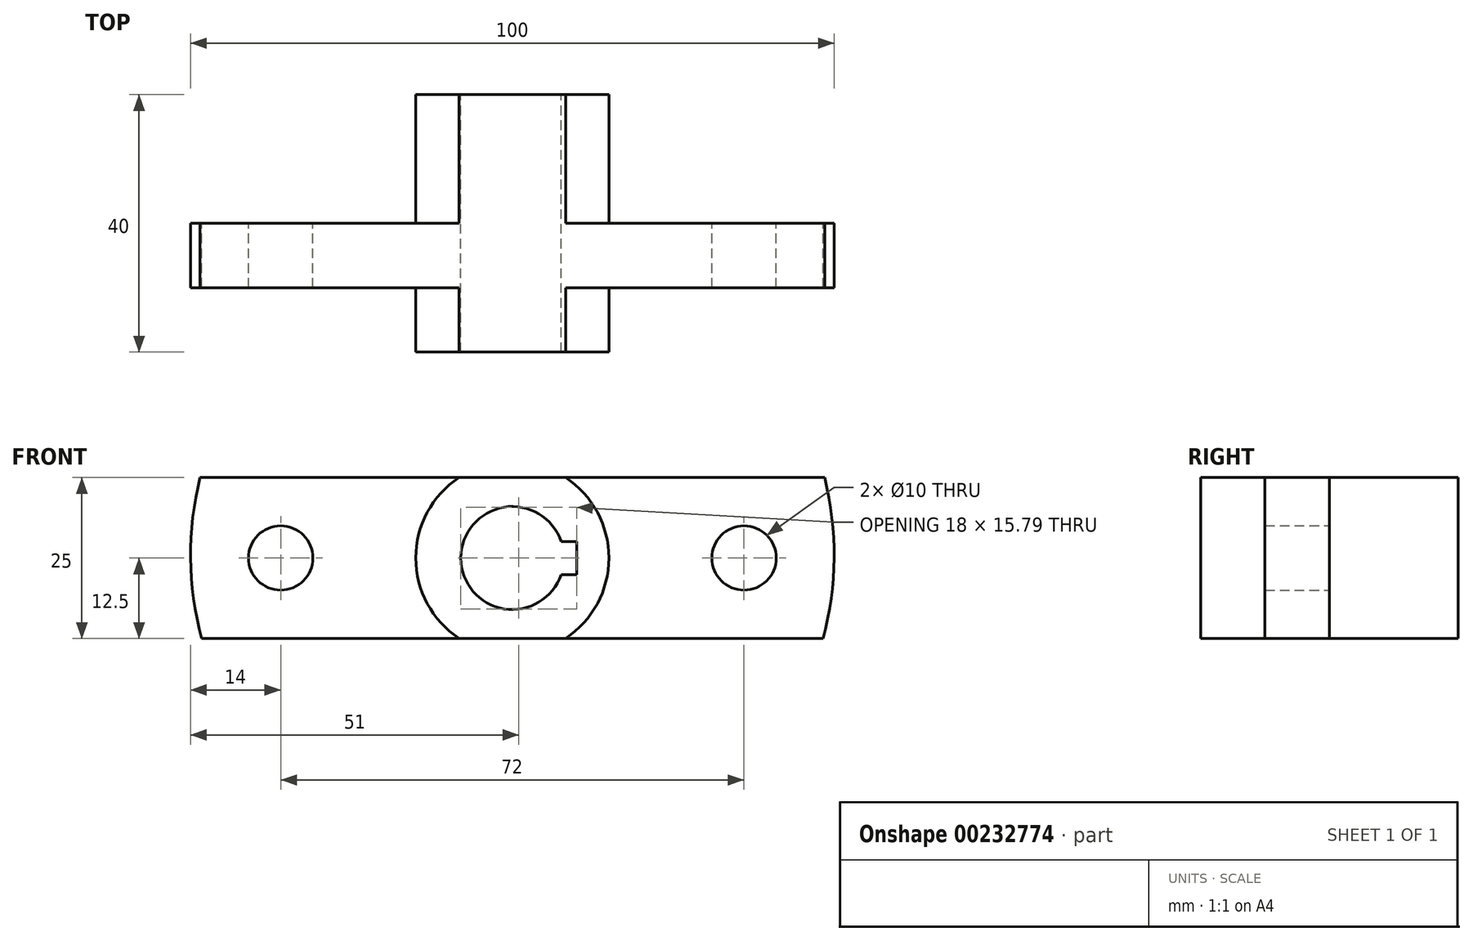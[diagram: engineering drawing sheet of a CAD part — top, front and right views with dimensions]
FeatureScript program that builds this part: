
annotation { "Feature Type Name" : "Feature", "Feature Type Description" : "" }
export const myFeature = defineFeature(function(context is Context, id is Id, definition is map)
    precondition{}
    {
        {
            var Q0;
            Q0=qCreatedBy(makeId("Front.planeOp"),FACE);
            var sketch = newSketch(context, id + "F0", { "sketchPlane" : qUnion([Q0])});
            skArc(sketch, "E0", {"start": v(7.58, 2.56) * mm, "mid": v(-8, 0) * mm, "end": v(7.58, -2.56) * mm});
            skArc(sketch, "E1", {"start": v(-8.3, 12.5) * mm, "mid": v(-15, 0) * mm, "end": v(-8.3, -12.5) * mm});
            skCircle(sketch, "E2", {"center": v(36, 0) * mm, "radius": 5 * mm});
            skArc(sketch, "E3", {"start": v(-48.53, 12.5) * mm, "mid": v(-50, -0.01) * mm, "end": v(-48.3, -12.5) * mm});
            skCircle(sketch, "E4", {"center": v(-36, 0) * mm, "radius": 5 * mm});
            skLineSegment(sketch, "E5", {"start": v(7.58, 2.56) * mm, "end": v(10, 2.56) * mm});
            skLineSegment(sketch, "E6", {"start": v(10, 2.56) * mm, "end": v(10, -2.56) * mm});
            skLineSegment(sketch, "E7", {"start": v(10, -2.56) * mm, "end": v(7.58, -2.56) * mm});
            skLineSegment(sketch, "E8", {"start": v(48.53, 12.5) * mm, "end": v(-48.53, 12.5) * mm});
            skLineSegment(sketch, "E9", {"start": v(48.3, -12.5) * mm, "end": v(-48.3, -12.5) * mm});
            skArc(sketch, "E10.trimOffspring", {"start": v(48.3, -12.5) * mm, "mid": v(50, -0.01) * mm, "end": v(48.53, 12.5) * mm});
            skArc(sketch, "E11.trimOffspring", {"start": v(8.3, -12.5) * mm, "mid": v(15, 0) * mm, "end": v(8.3, 12.5) * mm});
            skSolve(sketch);
        }
        {
            var Q0;
            Q0=makeQuery(id+"F0.imprint","IMPRINT",FACE,{"disambiguationData":[TD([[makeQuery(id+"F0.imprint","IMPRINT",EDGE,{"derivedFrom":sQuery(id+"F0.wireOp",EDGE,"E0")}),-1.0]])]});
            extrude(context, id + "F1", {"entities" : qUnion([Q0]), "depth" : 40 * mm});
        }
        {
            var Q0;
            {var subQ1=sQuery(id+"F0.wireOp",EDGE,"E1");Q0=makeQuery(id+"F0.imprint","IMPRINT",FACE,{"disambiguationData":[TD([[makeQuery(id+"F0.imprint","IMPRINT",EDGE,{"derivedFrom":subQ1}),-1.0]])]});}
            var Q1;
            Q1=makeQuery(id+"F0.imprint","IMPRINT",FACE,{"disambiguationData":[TD([[makeQuery(id+"F0.imprint","IMPRINT",EDGE,{"derivedFrom":sQuery(id+"F0.wireOp",EDGE,"E2")}),-1.0]])]});
            extrude(context, id + "F2", {"entities" : qUnion([Q0, Q1]), "operationType" : NewBodyOperationType.ADD, "depth" : 30 * mm, "hasSecondDirection" : true, "secondDirectionOppositeDirection" : false, "secondDirectionDepth" : 20 * mm});
        }
    });
